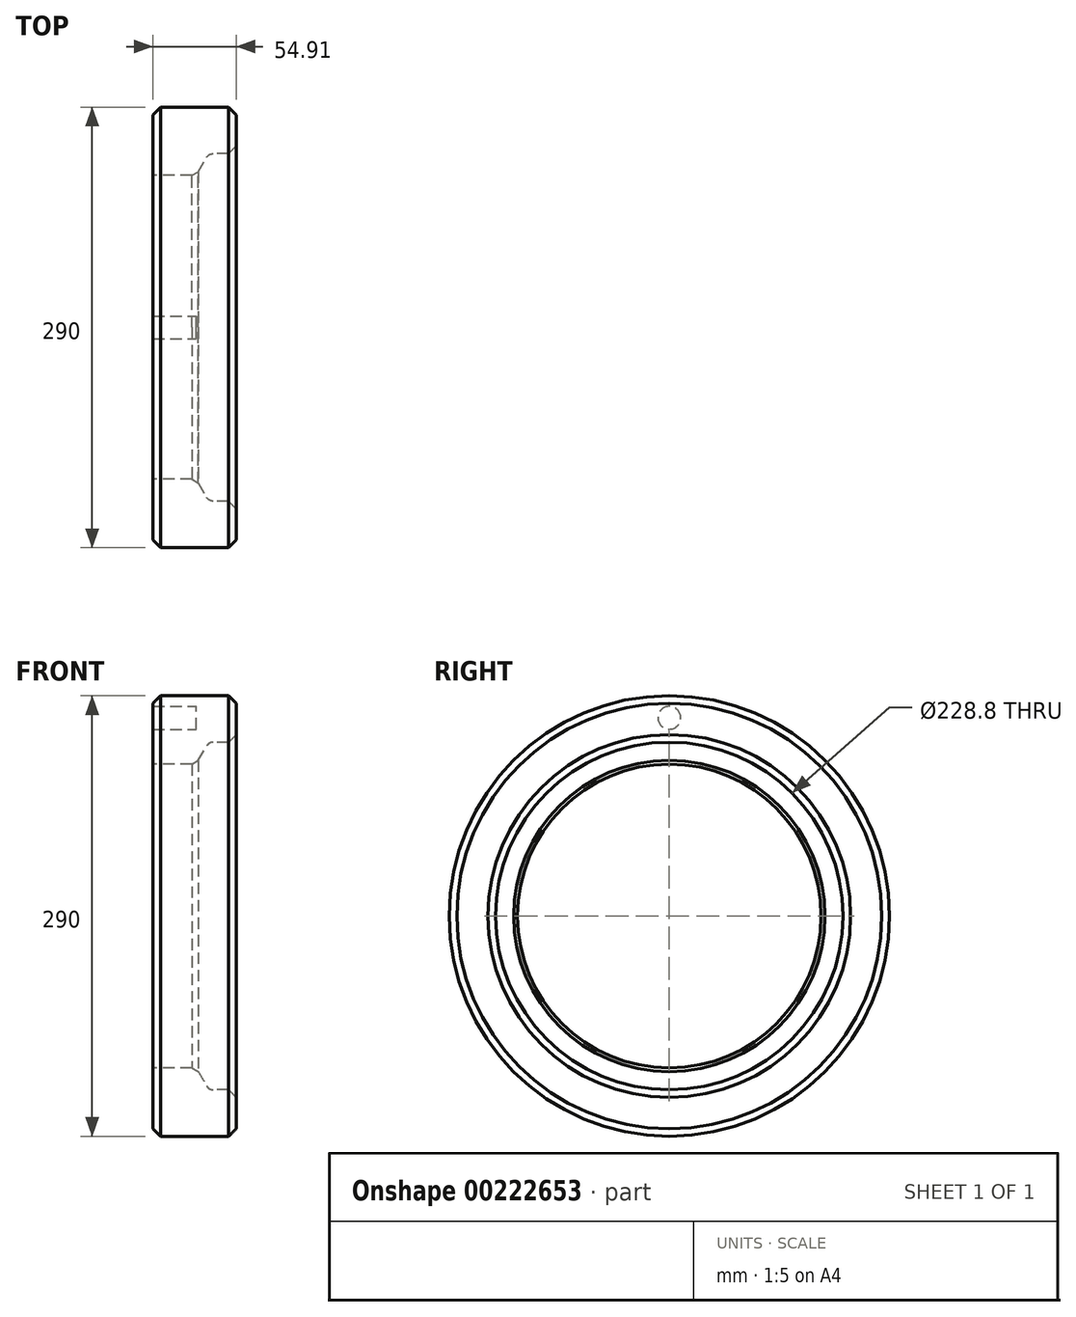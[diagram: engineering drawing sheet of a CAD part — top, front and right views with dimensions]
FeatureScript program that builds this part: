
annotation { "Feature Type Name" : "Feature", "Feature Type Description" : "" }
export const myFeature = defineFeature(function(context is Context, id is Id, definition is map)
    precondition{}
    {
        {
            var Q0;
            Q0=qCreatedBy(makeId("Front.planeOp"),FACE);
            var sketch = newSketch(context, id + "F0", { "sketchPlane" : qUnion([Q0])});
            skLineSegment(sketch, "E0", {"start": v(-27.22, 145) * mm, "end": v(26.33, 145) * mm});
            skLineSegment(sketch, "E1", {"start": v(26.33, 145) * mm, "end": v(26.33, 114.4) * mm});
            skLineSegment(sketch, "E2", {"start": v(26.33, 114.4) * mm, "end": v(8.33, 114.4) * mm});
            skLineSegment(sketch, "E3", {"start": v(8.33, 114.4) * mm, "end": v(0, 100) * mm});
            skLineSegment(sketch, "E4", {"start": v(0, 100) * mm, "end": v(-28.58, 100) * mm});
            skLineSegment(sketch, "E5", {"start": v(-28.58, 100) * mm, "end": v(-28.58, 145) * mm});
            skLineSegment(sketch, "E6", {"start": v(-71.78, 0) * mm, "end": v(69.07, 0) * mm});
            skLineSegment(sketch, "E7", {"start": v(-28.58, 145) * mm, "end": v(-27.22, 145) * mm});
            skSolve(sketch);
        }
        {
            var Q0;
            Q0 = qSketchRegion(id + "F0", true);
            var Q1;
            Q1=sQuery(id+"F0.wireOp",EDGE,"E6");
            revolve(context, id + "F1", {"entities" : qUnion([Q0]), "axis" : qUnion([Q1]), "revolveType" : RevolveType.FULL});
        }
        {
            var Q0;
            Q0=makeQuery(id+"F1.opRevolve","SWEPT_EDGE",EDGE,{"disambiguationData":[OSD([sQuery(id+"F0.wireOp",EDGE,"E0"),sQuery(id+"F0.wireOp",EDGE,"E1")])]});
            var Q1;
            Q1=makeQuery(id+"F1.opRevolve","SWEPT_EDGE",EDGE,{"disambiguationData":[OSD([sQuery(id+"F0.wireOp",EDGE,"E1"),sQuery(id+"F0.wireOp",EDGE,"E2")])]});
            var Q2;
            Q2=makeQuery(id+"F1.opRevolve","SWEPT_EDGE",EDGE,{"disambiguationData":[OSD([sQuery(id+"F0.wireOp",EDGE,"E3"),sQuery(id+"F0.wireOp",EDGE,"E4")])]});
            var Q3;
            Q3=makeQuery(id+"F1.opRevolve","SWEPT_EDGE",EDGE,{"disambiguationData":[OSD([sQuery(id+"F0.wireOp",EDGE,"E5"),sQuery(id+"F0.wireOp",EDGE,"E7")])]});
            chamfer(context, id + "F2", {"entities" : qUnion([Q0, Q1, Q2, Q3]), "width" : 5 * mm, "tangentPropagation" : true});
        }
        {
            var Q0;
            Q0=makeQuery(id+"F1.opRevolve","SWEPT_EDGE",EDGE,{"disambiguationData":[OSD([sQuery(id+"F0.wireOp",EDGE,"E2"),sQuery(id+"F0.wireOp",EDGE,"E3")])]});
            fillet(context, id + "F3", {"entities" : qUnion([Q0]), "radius" : 5 * mm, "tangentPropagation" : true, "allowEdgeOverflow" : false});
        }
        {
            var Q0;
            Q0=qCreatedBy(makeId("Right.planeOp"),FACE);
            var sketch = newSketch(context, id + "F4", { "sketchPlane" : qUnion([Q0])});
            skCircle(sketch, "E8", {"center": v(0, 130.47) * mm, "radius": 4.02 * mm});
            skSolve(sketch);
        }
        {
            var Q0;
            Q0=sQuery(id+"F4.wireOp",VERTEX,"E8.center");
            var Q1;
            Q1=makeQuery(id+"F1.opRevolve","SWEPT_BODY",BODY,{"disambiguationData":[OSD([sQuery(id+"F0.wireOp",EDGE,"E0"),sQuery(id+"F0.wireOp",EDGE,"E1"),sQuery(id+"F0.wireOp",EDGE,"E2"),sQuery(id+"F0.wireOp",EDGE,"E3"),sQuery(id+"F0.wireOp",EDGE,"E4"),sQuery(id+"F0.wireOp",EDGE,"E5"),sQuery(id+"F0.wireOp",EDGE,"E7")])]});
            hole(context, id + "F5", {"style" : HoleStyle.SIMPLE, "endStyle" : HoleEndStyle.THROUGH, "holeDiameter" : 15 * mm, "locations" : qUnion([Q0]), "scope" : qUnion([Q1]), "isTappedThrough" : true});
        }
    });
